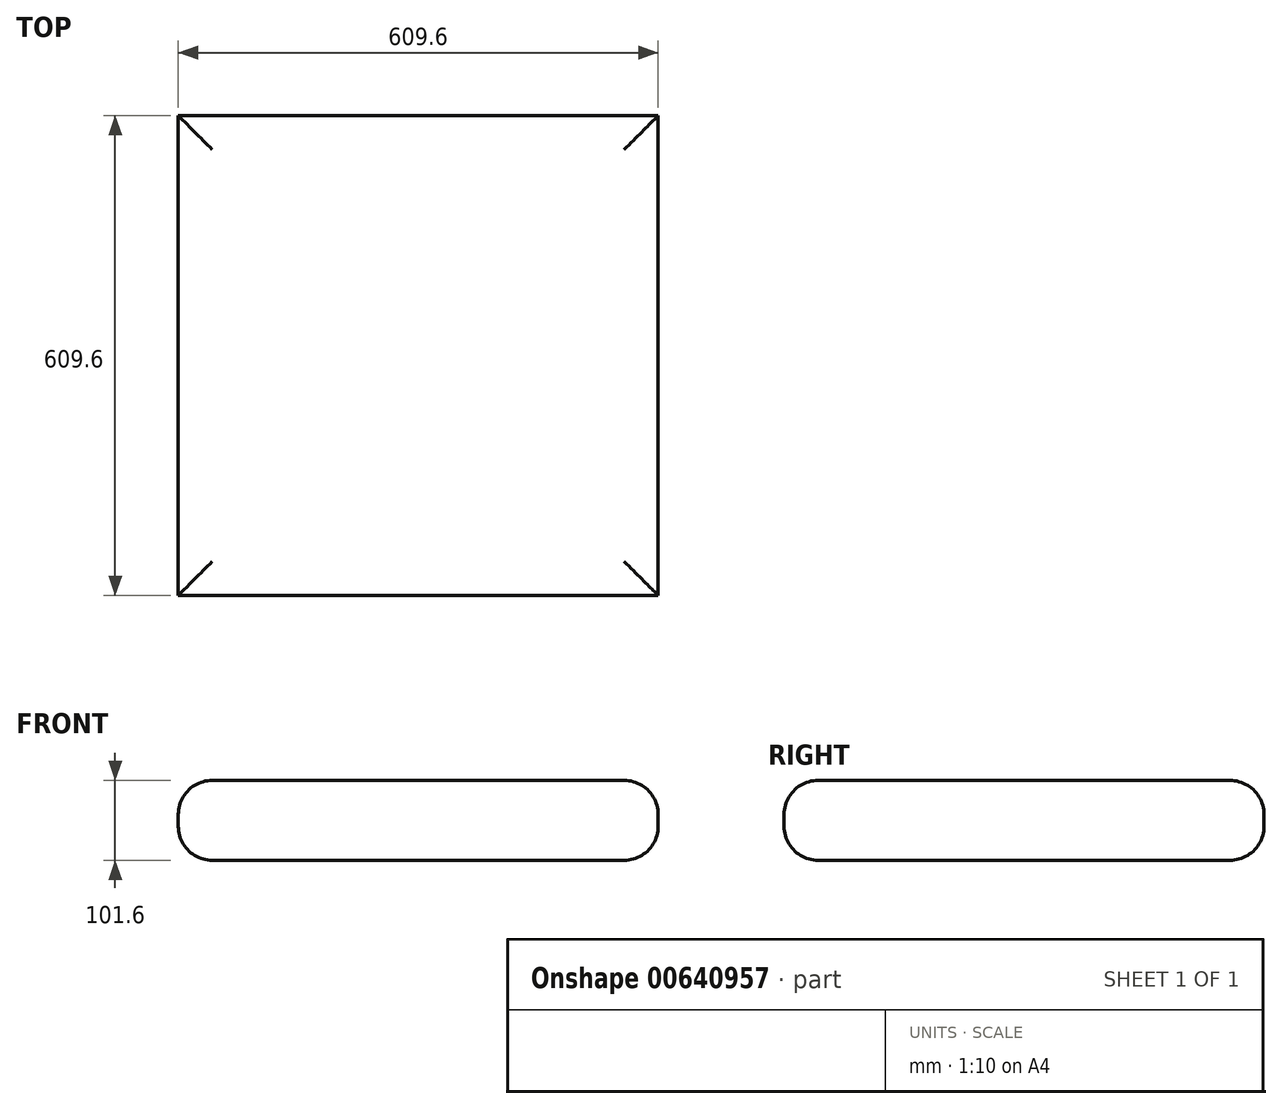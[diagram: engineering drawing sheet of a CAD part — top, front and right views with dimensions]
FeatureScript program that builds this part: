
annotation { "Feature Type Name" : "Feature", "Feature Type Description" : "" }
export const myFeature = defineFeature(function(context is Context, id is Id, definition is map)
    precondition{}
    {
        {
            var Q0;
            Q0=qCreatedBy(makeId("Top.planeOp"),FACE);
            var sketch = newSketch(context, id + "F0", { "sketchPlane" : qUnion([Q0])});
            skLineSegment(sketch, "E0.bottom", {"start": v(-601.94, 634.75) * mm, "end": v(7.66, 634.75) * mm});
            skLineSegment(sketch, "E0.top", {"start": v(-601.94, 25.15) * mm, "end": v(7.66, 25.15) * mm});
            skLineSegment(sketch, "E0.left", {"start": v(-601.94, 634.75) * mm, "end": v(-601.94, 25.15) * mm});
            skLineSegment(sketch, "E0.right", {"start": v(7.66, 634.75) * mm, "end": v(7.66, 25.15) * mm});
            skSolve(sketch);
        }
        {
            var Q0;
            Q0=qSketchRegion(id+"F0",true);
            extrude(context, id + "F1", {"entities" : qUnion([Q0]), "depth" : 101.6 * mm});
        }
        {
            var Q0;
            Q0=makeQuery(id+"F1.opExtrude","CAP_FACE",FACE,{"disambiguationData":[OSD([sQuery(id+"F0.wireOp",EDGE,"E0.bottom"),sQuery(id+"F0.wireOp",EDGE,"E0.top"),sQuery(id+"F0.wireOp",EDGE,"E0.left"),sQuery(id+"F0.wireOp",EDGE,"E0.right")])],"isStart":false});
            var Q1;
            Q1=makeQuery(id+"F1.opExtrude","CAP_FACE",FACE,{"disambiguationData":[OSD([sQuery(id+"F0.wireOp",EDGE,"E0.bottom"),sQuery(id+"F0.wireOp",EDGE,"E0.top"),sQuery(id+"F0.wireOp",EDGE,"E0.left"),sQuery(id+"F0.wireOp",EDGE,"E0.right")])],"isStart":true});
            fillet(context, id + "F2", {"entities" : qUnion([Q0, Q1]), "radius" : 43.18 * mm, "tangentPropagation" : true, "allowEdgeOverflow" : false});
        }
    });
